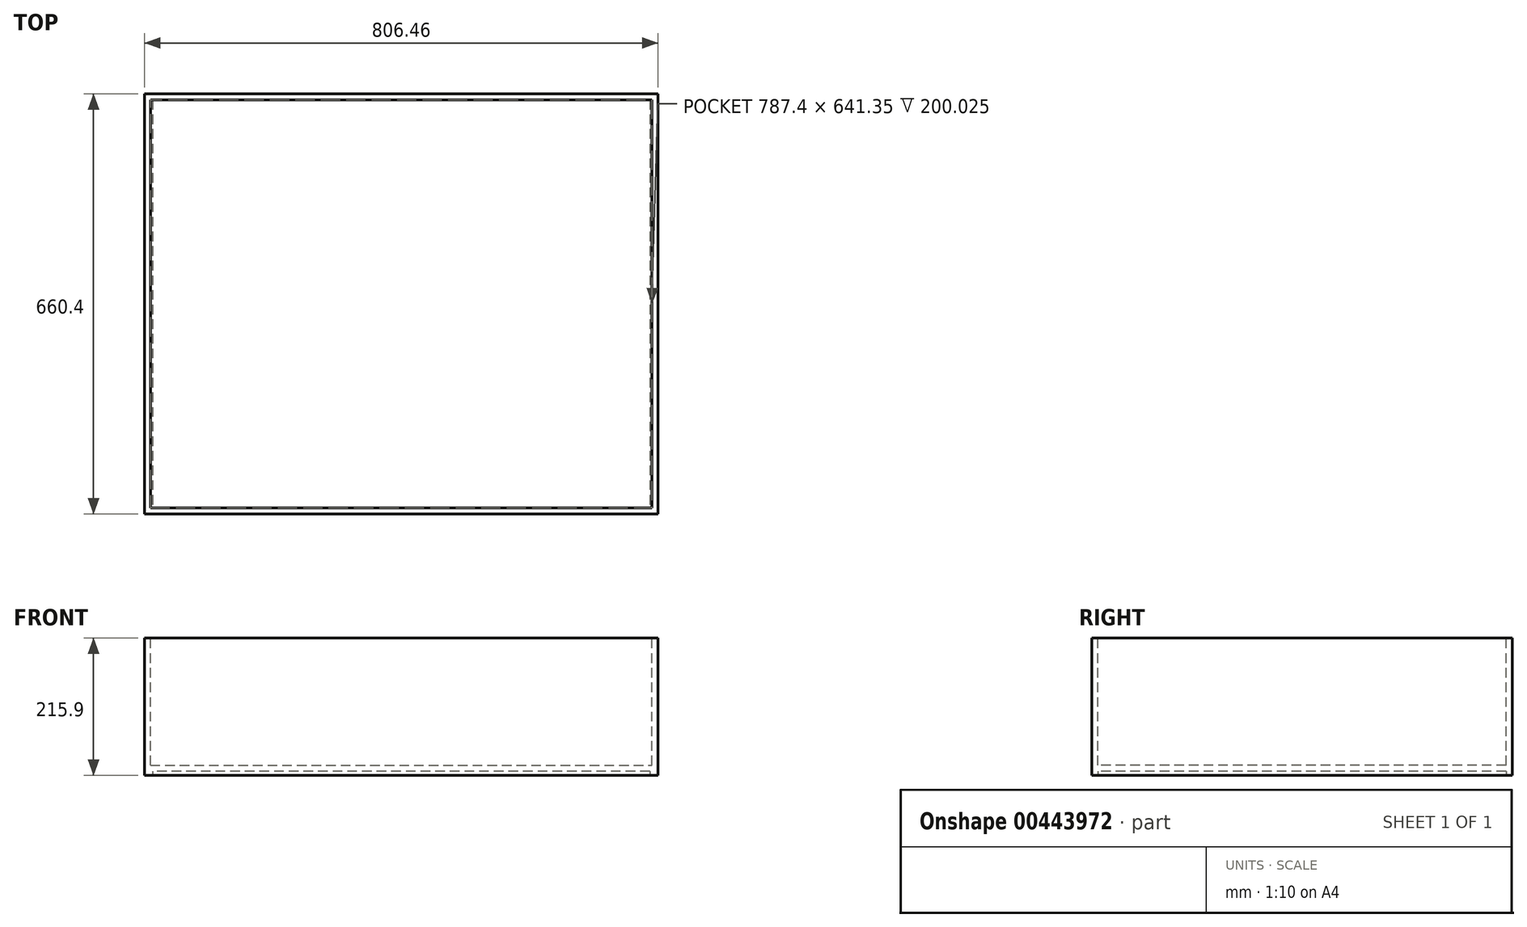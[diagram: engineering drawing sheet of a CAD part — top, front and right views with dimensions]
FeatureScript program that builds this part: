
annotation { "Feature Type Name" : "Feature", "Feature Type Description" : "" }
export const myFeature = defineFeature(function(context is Context, id is Id, definition is map)
    precondition{}
    {
        {
            var Q0;
            Q0=qCreatedBy(makeId("Front.planeOp"),FACE);
            var sketch = newSketch(context, id + "F0", { "sketchPlane" : qUnion([Q0])});
            skLineSegment(sketch, "E0.bottom", {"start": v(403.23, -107.95) * mm, "end": v(-403.23, -107.95) * mm});
            skLineSegment(sketch, "E0.top", {"start": v(403.23, 107.95) * mm, "end": v(-403.23, 107.95) * mm});
            skLineSegment(sketch, "E0.left", {"start": v(403.23, -107.95) * mm, "end": v(403.23, 107.95) * mm});
            skLineSegment(sketch, "E0.right", {"start": v(-403.23, -107.95) * mm, "end": v(-403.23, 107.95) * mm});
            skPoint(sketch, "E0.middle", {"position": v(0, 0) * mm});
            skSolve(sketch);
        }
        {
            var Q0;
            Q0=makeQuery(id+"F0.imprint","IMPRINT",FACE,{"disambiguationData":[TD([[makeQuery(id+"F0.imprint","IMPRINT",EDGE,{"derivedFrom":sQuery(id+"F0.wireOp",EDGE,"E0.bottom")}),-1.0]])]});
            extrude(context, id + "F1", {"entities" : qUnion([Q0]), "depth" : 660.4 * mm});
        }
        {
            var Q0;
            Q0=makeQuery(id+"F1.opExtrude","SWEPT_FACE",FACE,{"disambiguationData":[OSD([sQuery(id+"F0.wireOp",EDGE,"E0.bottom")])]});
            var sketch = newSketch(context, id + "F2", { "sketchPlane" : qUnion([Q0])});
            skLineSegment(sketch, "E1.bottom", {"start": v(390.53, 9.52) * mm, "end": v(-390.53, 9.52) * mm});
            skLineSegment(sketch, "E1.top", {"start": v(390.53, 650.88) * mm, "end": v(-390.53, 650.88) * mm});
            skLineSegment(sketch, "E1.left", {"start": v(390.52, 9.53) * mm, "end": v(390.53, 650.88) * mm});
            skLineSegment(sketch, "E1.right", {"start": v(-390.53, 9.52) * mm, "end": v(-390.52, 650.88) * mm});
            skPoint(sketch, "E1.middle", {"position": v(0, 330.2) * mm});
            skSolve(sketch);
        }
        {
            var Q0;
            Q0=makeQuery(id+"F2.imprint","IMPRINT",FACE,{"disambiguationData":[TD([[makeQuery(id+"F2.imprint","IMPRINT",EDGE,{"derivedFrom":sQuery(id+"F2.wireOp",EDGE,"E1.bottom")}),-1.0]])]});
            extrude(context, id + "F3", {"entities" : qUnion([Q0]), "operationType" : NewBodyOperationType.REMOVE, "oppositeDirection" : true, "depth" : 6.35 * mm});
        }
        {
            var Q0;
            Q0=makeQuery(id+"F1.opExtrude","SWEPT_FACE",FACE,{"disambiguationData":[OSD([sQuery(id+"F0.wireOp",EDGE,"E0.top")])]});
            shell(context, id + "F4", {"entities" : qUnion([Q0]), "thickness" : 9.52 * mm});
        }
    });
